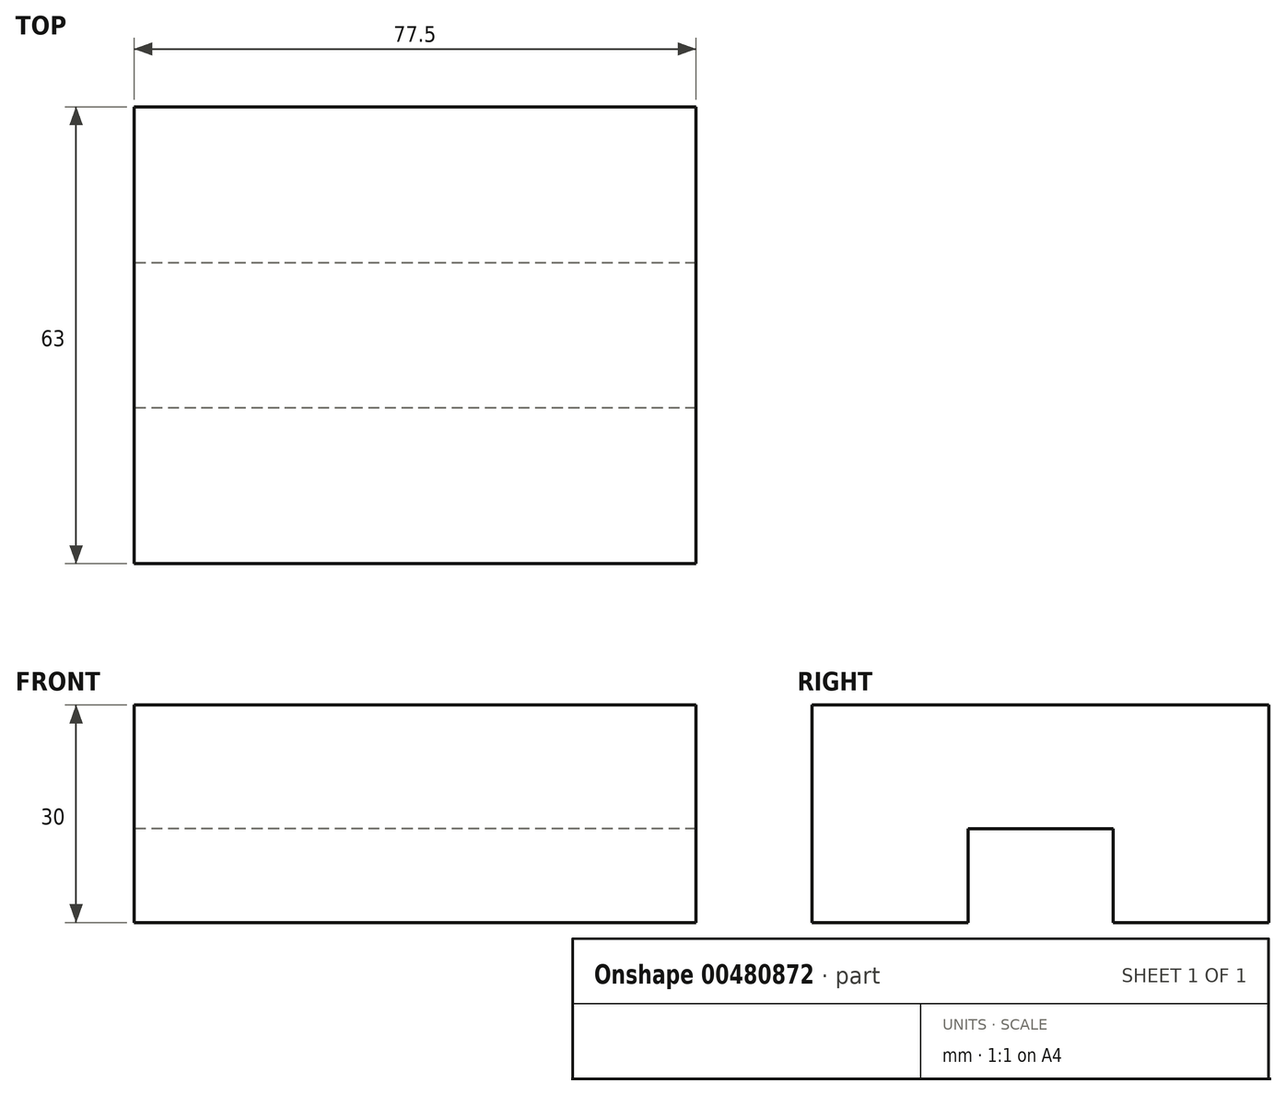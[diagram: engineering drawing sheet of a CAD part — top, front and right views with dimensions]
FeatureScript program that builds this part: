
annotation { "Feature Type Name" : "Feature", "Feature Type Description" : "" }
export const myFeature = defineFeature(function(context is Context, id is Id, definition is map)
    precondition{}
    {
        {
            var Q0;
            Q0=qCreatedBy(makeId("Right.planeOp"),FACE);
            var sketch = newSketch(context, id + "F0", { "sketchPlane" : qUnion([Q0])});
            skLineSegment(sketch, "E0.bottom", {"start": v(31.5, -15) * mm, "end": v(-31.5, -15) * mm});
            skLineSegment(sketch, "E0.top", {"start": v(31.5, 15) * mm, "end": v(-31.5, 15) * mm});
            skLineSegment(sketch, "E0.left", {"start": v(31.5, -15) * mm, "end": v(31.5, 15) * mm});
            skLineSegment(sketch, "E0.right", {"start": v(-31.5, -15) * mm, "end": v(-31.5, 15) * mm});
            skPoint(sketch, "E0.middle", {"position": v(0, 0) * mm});
            skLineSegment(sketch, "E1", {"start": v(-10, -2.1) * mm, "end": v(10, -2.1) * mm});
            skPoint(sketch, "E2", {"position": v(0, -2.1) * mm});
            skLineSegment(sketch, "E3", {"start": v(-10, -2.1) * mm, "end": v(-10, -15) * mm});
            skLineSegment(sketch, "E4", {"start": v(10, -2.1) * mm, "end": v(10, -15) * mm});
            skSolve(sketch);
        }
        {
            var Q0;
            Q0=makeQuery(id+"F0.imprint","IMPRINT",FACE,{"disambiguationData":[TD([[makeQuery(id+"F0.imprint","IMPRINT",EDGE,{"derivedFrom":sQuery(id+"F0.wireOp",EDGE,"E0.top")}),1.0]])]});
            extrude(context, id + "F1", {"entities" : qUnion([Q0]), "depth" : 77.5 * mm});
        }
    });
